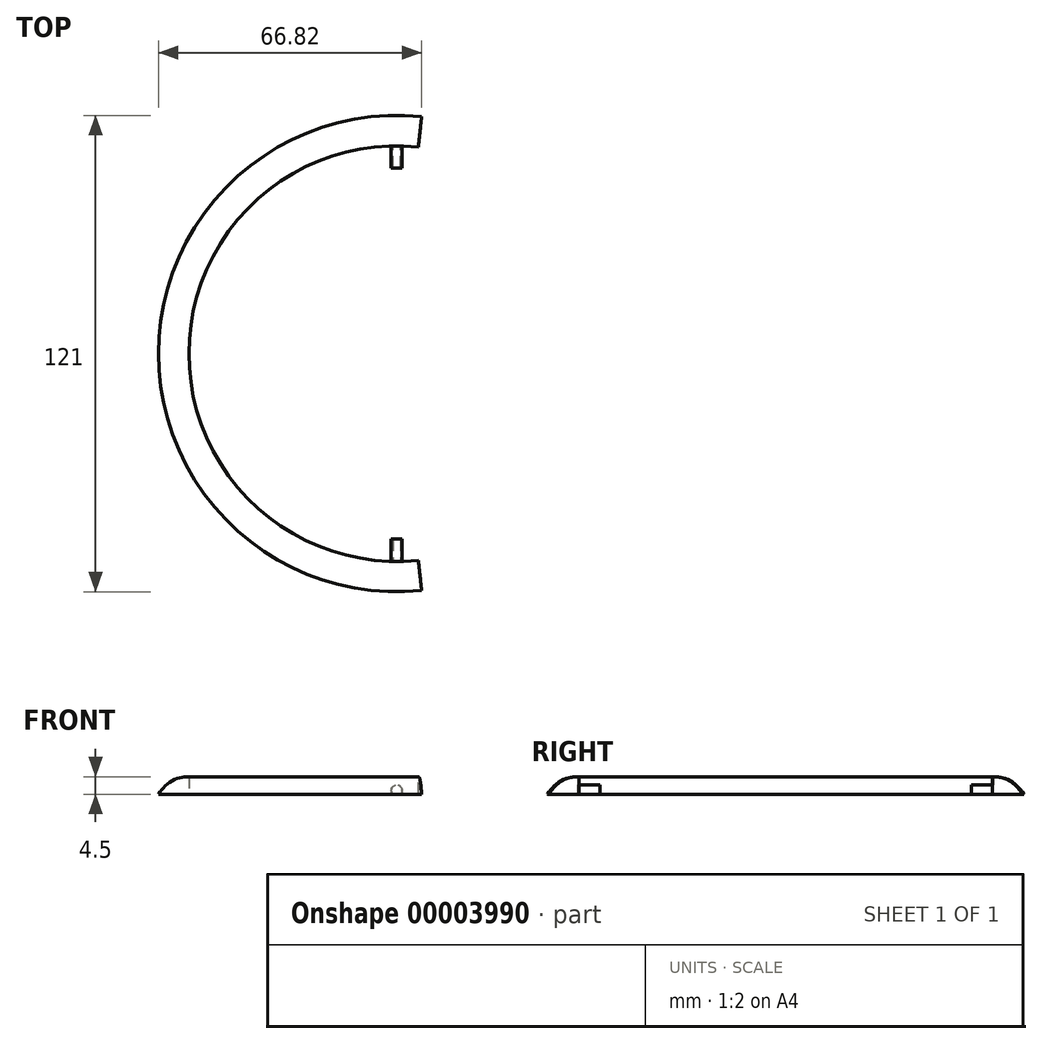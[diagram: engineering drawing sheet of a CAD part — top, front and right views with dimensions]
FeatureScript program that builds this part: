
annotation { "Feature Type Name" : "Feature", "Feature Type Description" : "" }
export const myFeature = defineFeature(function(context is Context, id is Id, definition is map)
    precondition{}
    {
        {
            var Q0;
            Q0=qCreatedBy(makeId("Top.planeOp"),FACE);
            var sketch = newSketch(context, id + "F0", { "sketchPlane" : qUnion([Q0])});
            skCircle(sketch, "E0", {"center": v(0, 0) * mm, "radius": 52.8 * mm, "construction": true});
            skLineSegment(sketch, "E1", {"start": v(-6, 52.46) * mm, "end": v(6, 52.46) * mm, "construction": true});
            skLineSegment(sketch, "E2", {"start": v(0, 52.46) * mm, "end": v(0, 47.15) * mm, "construction": true});
            skSolve(sketch);
        }
        {
            var Q0;
            Q0=qCreatedBy(makeId("Right.planeOp"),FACE);
            var sketch = newSketch(context, id + "F1", { "sketchPlane" : qUnion([Q0])});
            skLineSegment(sketch, "E3.0", {"start": v(-52.8, 0) * mm, "end": v(52.8, 0) * mm, "construction": true});
            skLineSegment(sketch, "E4", {"start": v(52.8, 0) * mm, "end": v(58.1, 0) * mm});
            skLineSegment(sketch, "E5", {"start": v(58.1, 0) * mm, "end": v(58.1, -1) * mm});
            skLineSegment(sketch, "E6", {"start": v(58.1, -1) * mm, "end": v(60.5, -1) * mm});
            skLineSegment(sketch, "E7", {"start": v(52.8, 0) * mm, "end": v(52.8, 3.5) * mm});
            skArc(sketch, "E8", {"start": v(60.5, -1) * mm, "mid": v(57.29, 2.34) * mm, "end": v(52.8, 3.5) * mm});
            skLineSegment(sketch, "E9", {"start": v(0, 0) * mm, "end": v(0, 33.28) * mm, "construction": true});
            skLineSegment(sketch, "E10", {"start": v(52.8, 0) * mm, "end": v(52.8, -1) * mm});
            skLineSegment(sketch, "E11", {"start": v(52.8, -1) * mm, "end": v(58.1, -1) * mm});
            skSolve(sketch);
        }
        {
            var Q0;
            Q0=makeQuery(id+"F1.imprint","IMPRINT",FACE,{"disambiguationData":[TD([[makeQuery(id+"F1.imprint","IMPRINT",EDGE,{"derivedFrom":sQuery(id+"F1.wireOp",EDGE,"E4")}),1.0]])]});
            var Q1;
            Q1=makeQuery(id+"F1.imprint","IMPRINT",FACE,{"disambiguationData":[TD([[makeQuery(id+"F1.imprint","IMPRINT",EDGE,{"derivedFrom":sQuery(id+"F1.wireOp",EDGE,"E4")}),-1.0]])]});
            var Q2;
            Q2=sQuery(id+"F1.wireOp",EDGE,"E9");
            revolve(context, id + "F2", {"entities" : qUnion([Q0, Q1]), "axis" : qUnion([Q2]), "revolveType" : RevolveType.TWO_DIRECTIONS, "angle" : 90 * degree, "angleBack" : 354 * degree});
        }
        {
            var Q0;
            Q0=qCreatedBy(makeId("Front.planeOp"),FACE);
            var Q1;
            Q1=sQuery(id+"F0.wireOp",VERTEX,"E2.end");
            cPlane(context, id + "F3", {"entities" : qUnion([Q0, Q1]), "cplaneType" : CPlaneType.PLANE_POINT, "offset" : 25 * mm, "width" : 150 * mm, "height" : 150 * mm});
        }
        {
            var Q0;
            Q0=qCreatedBy(id+"F3.planeOp",FACE);
            var sketch = newSketch(context, id + "F4", { "sketchPlane" : qUnion([Q0])});
            skCircle(sketch, "E12", {"center": v(0, 0) * mm, "radius": 1.4 * mm});
            skSolve(sketch);
        }
        {
            var Q0;
            Q0=makeQuery(id+"F4.imprint","IMPRINT",FACE,{"disambiguationData":[TD([[makeQuery(id+"F4.imprint","IMPRINT",EDGE,{"derivedFrom":sQuery(id+"F4.wireOp",EDGE,"E12")}),1.0]])]});
            extrude(context, id + "F5", {"entities" : qUnion([Q0]), "operationType" : NewBodyOperationType.ADD, "oppositeDirection" : true, "depth" : 8.9 * mm});
        }
        {
            var Q0;
            Q0=makeQuery(id+"F5.opExtrude","CAP_FACE",FACE,{"disambiguationData":[OSD([sQuery(id+"F4.wireOp",EDGE,"E12")])],"isStart":false});
            extrude(context, id + "F6", {"entities" : qUnion([Q0]), "operationType" : NewBodyOperationType.REMOVE, "endBound" : BoundingType.THROUGH_ALL, "oppositeDirection" : true, "depth" : 25 * mm});
        }
        {
            var Q0;
            Q0=makeQuery(id+"F2.opRevolve","SWEPT_BODY",BODY,{"disambiguationData":[OSD([sQuery(id+"F1.wireOp",EDGE,"E6"),sQuery(id+"F1.wireOp",EDGE,"E7"),sQuery(id+"F1.wireOp",EDGE,"E8"),sQuery(id+"F1.wireOp",EDGE,"E10"),sQuery(id+"F1.wireOp",EDGE,"E11")])]});
            var Q1;
            Q1=makeQuery(id+"F2.opRevolve","CAP_FACE",FACE,{"disambiguationData":[OSD([sQuery(id+"F1.wireOp",EDGE,"E6"),sQuery(id+"F1.wireOp",EDGE,"E7"),sQuery(id+"F1.wireOp",EDGE,"E8"),sQuery(id+"F1.wireOp",EDGE,"E10"),sQuery(id+"F1.wireOp",EDGE,"E11")])],"isStart":false});
            mirror(context, id + "F7", {"operationType" : NewBodyOperationType.ADD, "entities" : qUnion([Q0]), "mirrorPlane" : qUnion([Q1])});
        }
    });
